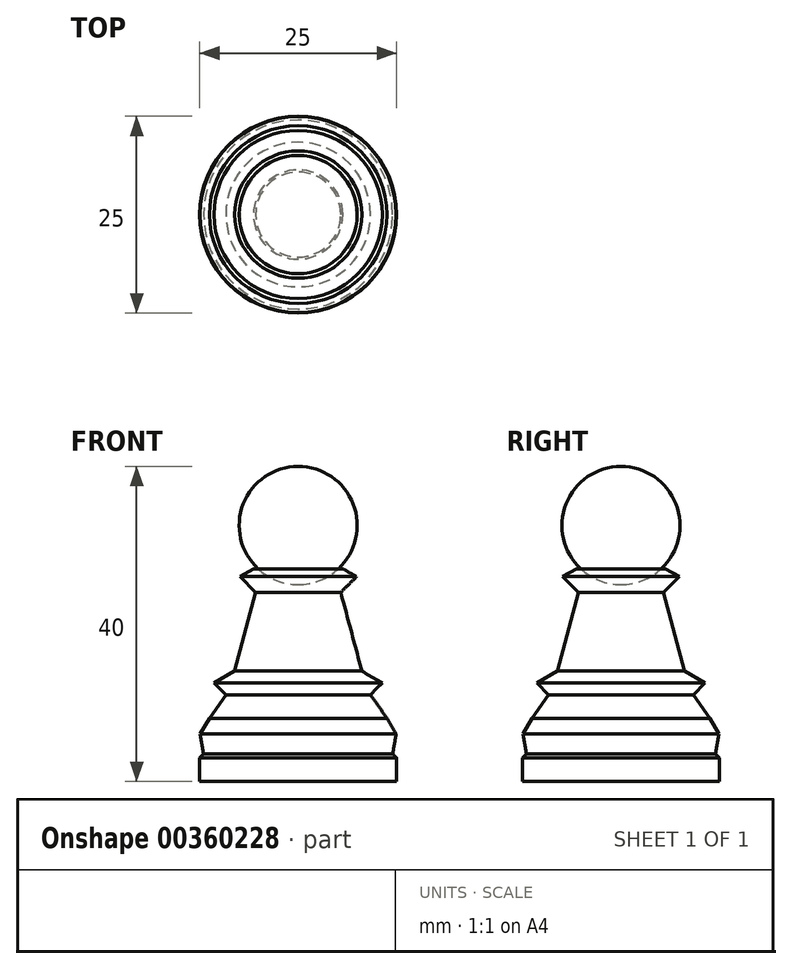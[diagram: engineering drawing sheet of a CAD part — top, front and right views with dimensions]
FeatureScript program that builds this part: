
annotation { "Feature Type Name" : "Feature", "Feature Type Description" : "" }
export const myFeature = defineFeature(function(context is Context, id is Id, definition is map)
    precondition{}
    {
        {
            var Q0;
            Q0=qCreatedBy(makeId("Top.planeOp"),FACE);
            var sketch = newSketch(context, id + "F0", { "sketchPlane" : qUnion([Q0])});
            skCircle(sketch, "E0", {"center": v(0, 0) * mm, "radius": 12.5 * mm});
            skSolve(sketch);
        }
        {
            var Q0;
            Q0=makeQuery(id+"F0.imprint","IMPRINT",FACE,{"disambiguationData":[TD([[makeQuery(id+"F0.imprint","IMPRINT",EDGE,{"derivedFrom":sQuery(id+"F0.wireOp",EDGE,"E0")}),1.0]])]});
            extrude(context, id + "F1", {"entities" : qUnion([Q0]), "depth" : 3 * mm});
        }
        {
            var Q0;
            Q0=makeQuery(id+"F1.opExtrude","CAP_FACE",FACE,{"disambiguationData":[OSD([sQuery(id+"F0.wireOp",EDGE,"E0")])],"isStart":false});
            extrude(context, id + "F2", {"entities" : qUnion([Q0]), "operationType" : NewBodyOperationType.ADD, "depth" : .5 * mm, "hasDraft" : true, "draftAngle" : 45 * degree, "draftPullDirection" : true});
        }
        {
            var Q0;
            Q0=makeQuery(id+"F2.opExtrude","CAP_FACE",FACE,{"disambiguationData":[OSD([sQuery(id+"F0.wireOp",EDGE,"E0")])],"isStart":false});
            extrude(context, id + "F3", {"entities" : qUnion([Q0]), "operationType" : NewBodyOperationType.ADD, "depth" : 2.5 * mm, "hasDraft" : true, "draftAngle" : 10 * degree});
        }
        {
            var Q0;
            Q0=makeQuery(id+"F3.opExtrude","CAP_FACE",FACE,{"disambiguationData":[OSD([sQuery(id+"F0.wireOp",EDGE,"E0")])],"isStart":false});
            extrude(context, id + "F4", {"entities" : qUnion([Q0]), "operationType" : NewBodyOperationType.ADD, "depth" : 2 * mm, "hasDraft" : true, "draftAngle" : 30 * degree, "draftPullDirection" : true});
        }
        {
            var Q0;
            Q0=makeQuery(id+"F4.opExtrude","CAP_FACE",FACE,{"disambiguationData":[OSD([sQuery(id+"F0.wireOp",EDGE,"E0")])],"isStart":false});
            extrude(context, id + "F5", {"entities" : qUnion([Q0]), "operationType" : NewBodyOperationType.ADD, "depth" : 3 * mm, "hasDraft" : true, "draftAngle" : 35 * degree, "draftPullDirection" : true});
        }
        {
            var Q0;
            Q0=makeQuery(id+"F5.opExtrude","CAP_FACE",FACE,{"disambiguationData":[OSD([sQuery(id+"F0.wireOp",EDGE,"E0")])],"isStart":false});
            extrude(context, id + "F6", {"entities" : qUnion([Q0]), "operationType" : NewBodyOperationType.ADD, "depth" : 1.5 * mm, "hasDraft" : true, "draftAngle" : 45 * degree});
        }
        {
            var Q0;
            Q0=makeQuery(id+"F6.opExtrude","CAP_FACE",FACE,{"disambiguationData":[OSD([sQuery(id+"F0.wireOp",EDGE,"E0")])],"isStart":false});
            extrude(context, id + "F7", {"entities" : qUnion([Q0]), "operationType" : NewBodyOperationType.ADD, "depth" : 1.5 * mm, "hasDraft" : true, "draftAngle" : 60 * degree, "draftPullDirection" : true});
        }
        {
            var Q0;
            Q0=makeQuery(id+"F7.opExtrude","CAP_FACE",FACE,{"disambiguationData":[OSD([sQuery(id+"F0.wireOp",EDGE,"E0")])],"isStart":false});
            extrude(context, id + "F8", {"entities" : qUnion([Q0]), "operationType" : NewBodyOperationType.ADD, "depth" : 10 * mm, "hasDraft" : true, "draftAngle" : 15 * degree, "draftPullDirection" : true});
        }
        {
            var Q0;
            Q0=makeQuery(id+"F8.opExtrude","CAP_FACE",FACE,{"disambiguationData":[OSD([sQuery(id+"F0.wireOp",EDGE,"E0")])],"isStart":false});
            extrude(context, id + "F9", {"entities" : qUnion([Q0]), "operationType" : NewBodyOperationType.ADD, "depth" : 2 * mm, "hasDraft" : true, "draftAngle" : 45 * degree});
        }
        {
            var Q0;
            Q0=makeQuery(id+"F9.opExtrude","CAP_FACE",FACE,{"disambiguationData":[OSD([sQuery(id+"F0.wireOp",EDGE,"E0")])],"isStart":false});
            extrude(context, id + "F10", {"entities" : qUnion([Q0]), "operationType" : NewBodyOperationType.ADD, "depth" : 1 * mm, "hasDraft" : true, "draftAngle" : 60 * degree, "draftPullDirection" : true});
        }
        {
            var Q0;
            Q0=qCreatedBy(makeId("Front.planeOp"),FACE);
            var sketch = newSketch(context, id + "F11", { "sketchPlane" : qUnion([Q0])});
            skLineSegment(sketch, "E1", {"start": v(0, 0) * mm, "end": v(0, 65) * mm});
            skCircle(sketch, "E2", {"center": v(0, 32.5) * mm, "radius": 7.5 * mm});
            skSolve(sketch);
        }
        {
            var Q0;
            {var subQ0=sQuery(id+"F11.wireOp",EDGE,"E2");var subQ1=sQuery(id+"F11.wireOp",EDGE,"E1");var subQ2=makeQuery(id+"F11.imprint","INTERSECT",VERTEX,{"disambiguationData":[OD(0.0)],"derivedFrom":[subQ1,subQ0]});Q0=makeQuery(id+"F11.imprint","IMPRINT",FACE,{"disambiguationData":[TD([[makeQuery(id+"F11.imprint","IMPRINT",EDGE,{"disambiguationData":[TD([[subQ2,-1.0]])],"derivedFrom":subQ1}),1.0]])]});}
            var Q1;
            Q1=sQuery(id+"F11.wireOp",EDGE,"E1");
            revolve(context, id + "F12", {"entities" : qUnion([Q0]), "axis" : qUnion([Q1]), "revolveType" : RevolveType.FULL});
        }
    });
